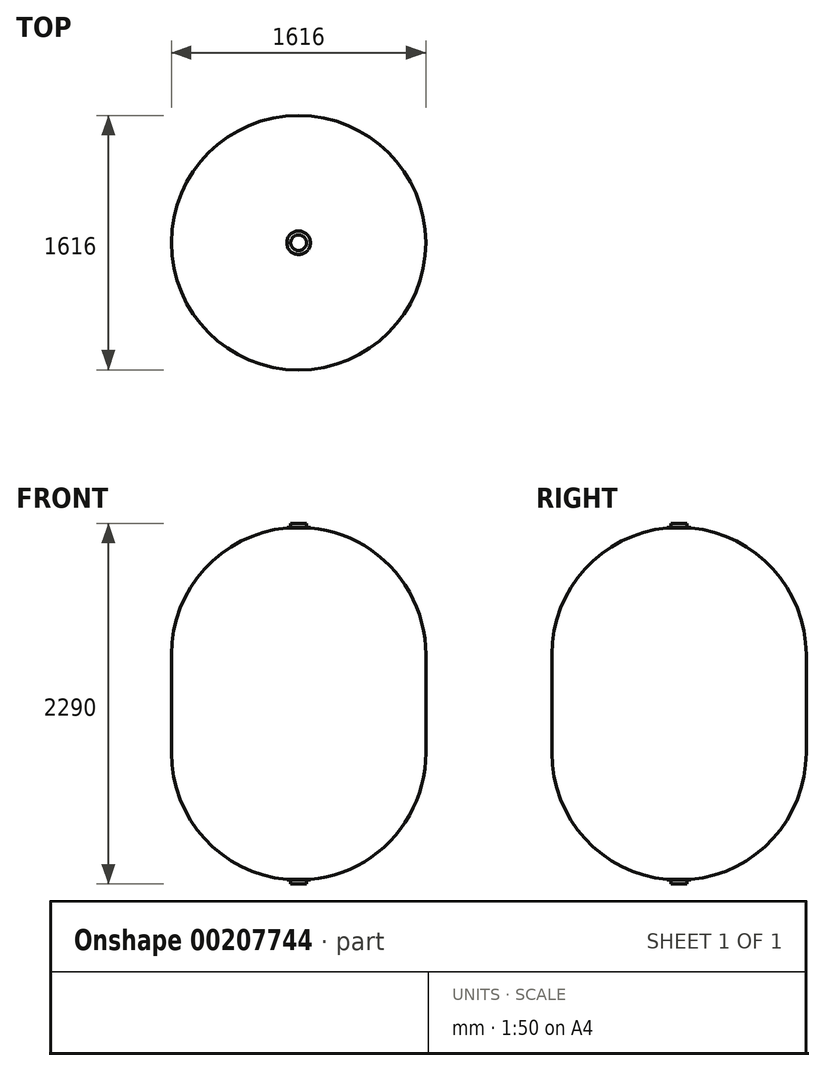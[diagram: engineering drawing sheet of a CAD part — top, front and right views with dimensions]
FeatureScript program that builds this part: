
annotation { "Feature Type Name" : "Feature", "Feature Type Description" : "" }
export const myFeature = defineFeature(function(context is Context, id is Id, definition is map)
    precondition{}
    {
        {
            var Q0;
            Q0=qCreatedBy(makeId("Front.planeOp"),FACE);
            var sketch = newSketch(context, id + "F0", { "sketchPlane" : qUnion([Q0])});
            skArc(sketch, "E0", {"start": v(75, 3.49) * mm, "mid": v(597.27, 263.82) * mm, "end": v(808, 808) * mm});
            skLineSegment(sketch, "E1", {"start": v(808, 808) * mm, "end": v(808, 1432) * mm});
            skArc(sketch, "E2", {"start": v(808, 1432) * mm, "mid": v(597.27, 1976.18) * mm, "end": v(75, 2236.51) * mm});
            skLineSegment(sketch, "E3", {"start": v(0, 2240) * mm, "end": v(0, 0) * mm});
            skLineSegment(sketch, "E4", {"start": v(75, 3.49) * mm, "end": v(75, 0) * mm});
            skLineSegment(sketch, "E5", {"start": v(75, 0) * mm, "end": v(50, 0) * mm});
            skLineSegment(sketch, "E6", {"start": v(50, 0) * mm, "end": v(50, -25) * mm});
            skLineSegment(sketch, "E7", {"start": v(50, -25) * mm, "end": v(0, -25) * mm});
            skLineSegment(sketch, "E8", {"start": v(0, -25) * mm, "end": v(0, 0) * mm});
            skLineSegment(sketch, "E9", {"start": v(75, 2236.51) * mm, "end": v(75, 2240) * mm});
            skLineSegment(sketch, "E10", {"start": v(75, 2240) * mm, "end": v(50, 2240) * mm});
            skLineSegment(sketch, "E11", {"start": v(50, 2240) * mm, "end": v(50, 2265) * mm});
            skLineSegment(sketch, "E12", {"start": v(50, 2265) * mm, "end": v(0, 2265) * mm});
            skLineSegment(sketch, "E13", {"start": v(0, 2265) * mm, "end": v(0, 2240) * mm});
            skSolve(sketch);
        }
        {
            var Q0;
            Q0=makeQuery(id+"F0.imprint","IMPRINT",FACE,{"disambiguationData":[TD([[makeQuery(id+"F0.imprint","IMPRINT",EDGE,{"derivedFrom":sQuery(id+"F0.wireOp",EDGE,"E0")}),1.0]])]});
            var Q1;
            Q1=sQuery(id+"F0.wireOp",EDGE,"E3");
            revolve(context, id + "F1", {"entities" : qUnion([Q0]), "axis" : qUnion([Q1]), "revolveType" : RevolveType.FULL});
        }
    });
